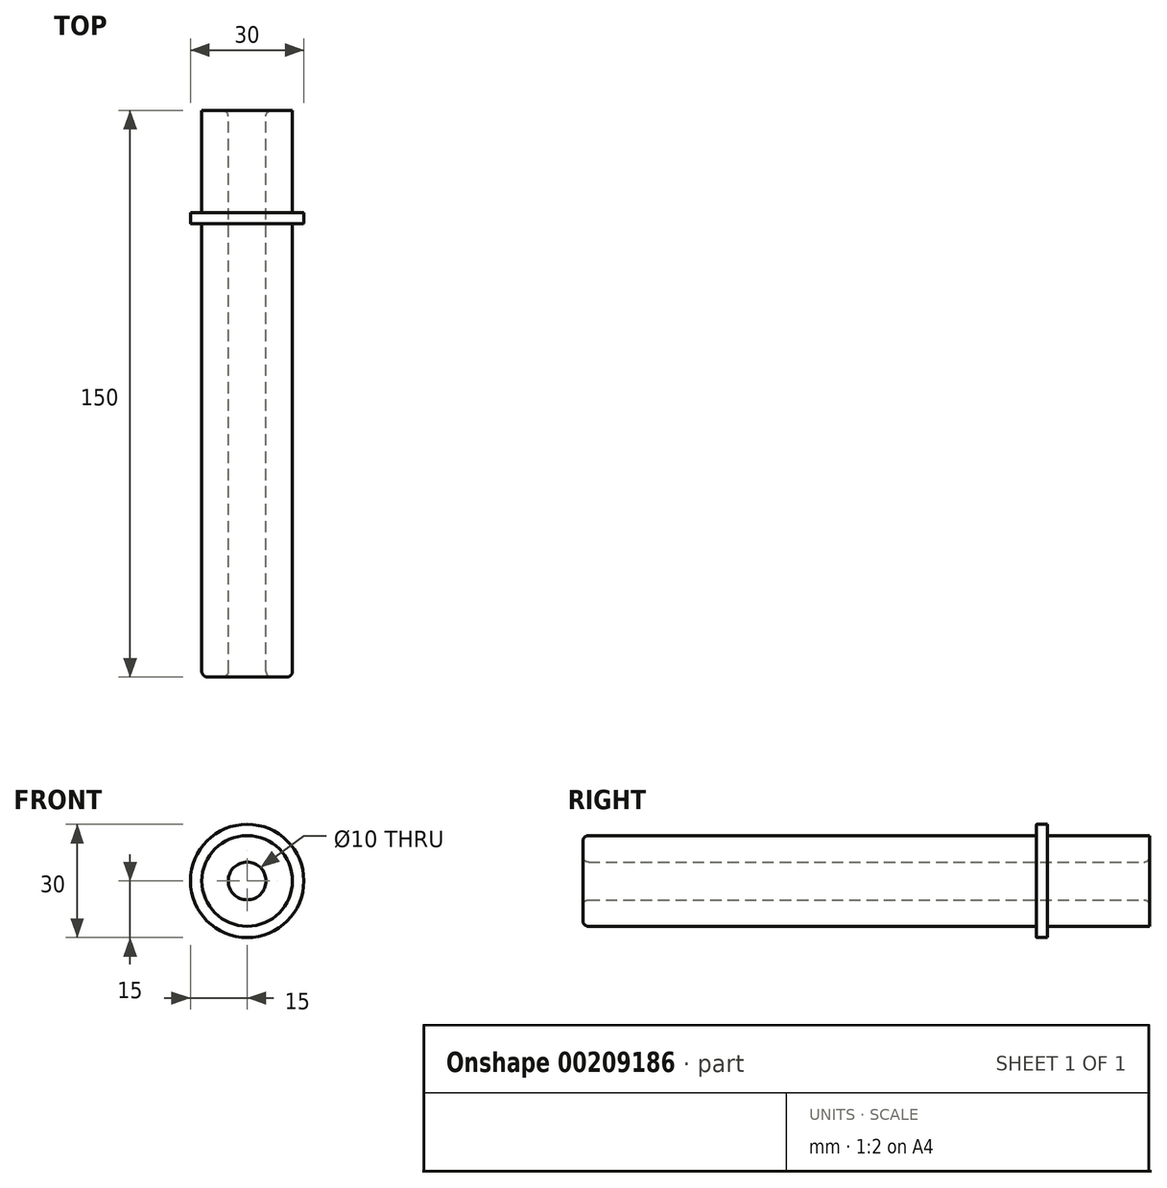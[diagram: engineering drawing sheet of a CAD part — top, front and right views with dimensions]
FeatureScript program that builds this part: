
annotation { "Feature Type Name" : "Feature", "Feature Type Description" : "" }
export const myFeature = defineFeature(function(context is Context, id is Id, definition is map)
    precondition{}
    {
        {
            var Q0;
            Q0=qCreatedBy(makeId("Front.planeOp"),FACE);
            var sketch = newSketch(context, id + "F0", { "sketchPlane" : qUnion([Q0])});
            skCircle(sketch, "E0", {"center": v(0, 0) * mm, "radius": 12 * mm});
            skCircle(sketch, "E1", {"center": v(0, 0) * mm, "radius": 15 * mm});
            skCircle(sketch, "E2", {"center": v(0, 0) * mm, "radius": 5 * mm});
            skSolve(sketch);
        }
        {
            var Q0;
            Q0=makeQuery(id+"F0.imprint","IMPRINT",FACE,{"disambiguationData":[TD([[makeQuery(id+"F0.imprint","IMPRINT",EDGE,{"derivedFrom":sQuery(id+"F0.wireOp",EDGE,"E0")}),1.0]])]});
            extrude(context, id + "F1", {"entities" : qUnion([Q0]), "depth" : 150 * mm});
        }
        {
            var Q0;
            Q0 = qSketchRegion(id + "F0", true);
            extrude(context, id + "F2", {"entities" : qUnion([Q0]), "operationType" : NewBodyOperationType.ADD, "depth" : 30 * mm});
        }
        {
            var Q0;
            Q0=makeQuery(id+"F0.imprint","IMPRINT",FACE,{"disambiguationData":[TD([[makeQuery(id+"F0.imprint","IMPRINT",EDGE,{"derivedFrom":sQuery(id+"F0.wireOp",EDGE,"E0")}),-1.0]])]});
            extrude(context, id + "F3", {"entities" : qUnion([Q0]), "operationType" : NewBodyOperationType.REMOVE, "depth" : 27 * mm});
        }
        {
            var Q0;
            Q0=makeQuery(id+"F2.opExtrude","CAP_EDGE",EDGE,{"disambiguationData":[OSD([sQuery(id+"F0.wireOp",EDGE,"E1")])],"isStart":false});
            var Q1;
            Q1=makeQuery(id+"F3.boolean.opBoolean","COPY",EDGE,{"derivedFrom":makeQuery(id+"F3.opExtrude","CAP_EDGE",EDGE,{"disambiguationData":[OSD([sQuery(id+"F0.wireOp",EDGE,"E1")])],"isStart":false})});
            fillet(context, id + "F4", {"entities" : qUnion([Q0, Q1]), "radius" : 0.25 * mm, "tangentPropagation" : true, "allowEdgeOverflow" : false});
        }
        {
            var Q0;
            Q0=makeQuery(id+"F3.boolean.opBoolean","COPY",EDGE,{"derivedFrom":makeQuery(id+"F3.opExtrude","CAP_EDGE",EDGE,{"disambiguationData":[OSD([sQuery(id+"F0.wireOp",EDGE,"E0")])],"isStart":true})});
            var Q1;
            Q1=makeQuery(id+"F1.opExtrude","CAP_EDGE",EDGE,{"disambiguationData":[OSD([sQuery(id+"F0.wireOp",EDGE,"E0")])],"isStart":false});
            var Q2;
            Q2=makeQuery(id+"F1.opExtrude","CAP_EDGE",EDGE,{"disambiguationData":[OSD([sQuery(id+"F0.wireOp",EDGE,"E2")])],"isStart":true});
            var Q3;
            Q3=makeQuery(id+"F1.opExtrude","CAP_EDGE",EDGE,{"disambiguationData":[OSD([sQuery(id+"F0.wireOp",EDGE,"E2")])],"isStart":false});
            fillet(context, id + "F5", {"entities" : qUnion([Q0, Q1, Q2, Q3]), "radius" : 1.5 * mm, "tangentPropagation" : true, "allowEdgeOverflow" : false});
        }
    });
